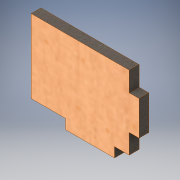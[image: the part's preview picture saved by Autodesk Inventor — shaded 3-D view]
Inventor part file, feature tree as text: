
AUTODESK INVENTOR PART (.ipt)
format: ipt  version: 2019 (Build 230136000, 136)  size: 129,024 bytes
history: native  units: mm
features: other x1, extrude x1, sketch x1
ambient origin geometry x8: Origin, YZ Plane, XZ Plane, XY Plane, X Axis, Y Axis, Z Axis, Center Point
bodies: Body1 (feature_tree)
feature tree (3):
  other  "Твердое тело1"
  extrude  "Выдавливание1"  Depth=4.0mm
  sketch  "Эскиз1"
